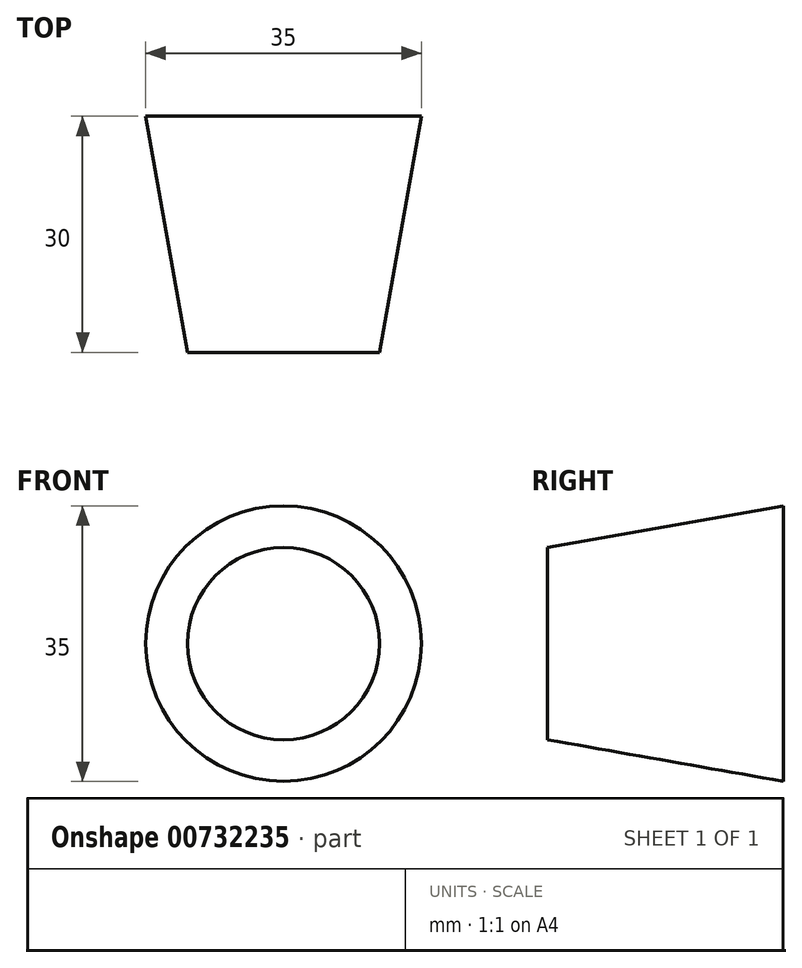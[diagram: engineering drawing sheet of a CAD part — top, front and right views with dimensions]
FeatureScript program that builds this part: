
annotation { "Feature Type Name" : "Feature", "Feature Type Description" : "" }
export const myFeature = defineFeature(function(context is Context, id is Id, definition is map)
    precondition{}
    {
        {
            var Q0;
            Q0=qCreatedBy(makeId("Front.planeOp"),FACE);
            var sketch = newSketch(context, id + "F0", { "sketchPlane" : qUnion([Q0])});
            skCircle(sketch, "E0", {"center": v(0, 0) * mm, "radius": 17.5 * mm});
            skSolve(sketch);
        }
        {
            var Q0;
            Q0=makeQuery(id+"F0.imprint","IMPRINT",FACE,{"disambiguationData":[TD([[makeQuery(id+"F0.imprint","IMPRINT",EDGE,{"derivedFrom":sQuery(id+"F0.wireOp",EDGE,"E0")}),1.0]])]});
            extrude(context, id + "F1", {"entities" : qUnion([Q0]), "depth" : 30 * mm, "offsetDistance" : 25 * mm, "hasDraft" : true, "draftAngle" : 10 * degree, "draftPullDirection" : true});
        }
    });
